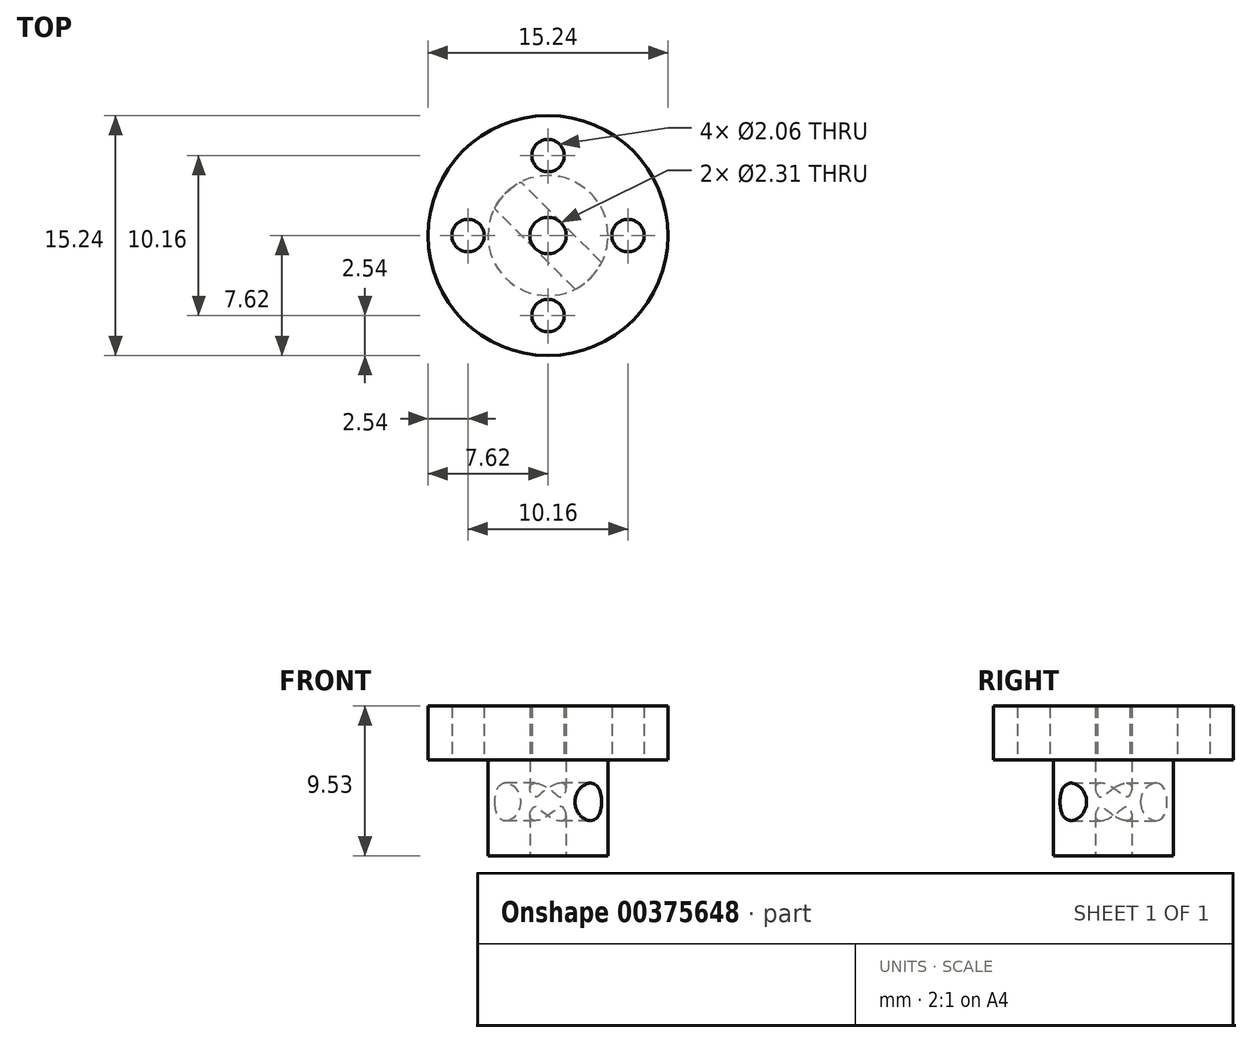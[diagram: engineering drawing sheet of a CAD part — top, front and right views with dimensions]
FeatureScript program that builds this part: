
annotation { "Feature Type Name" : "Feature", "Feature Type Description" : "" }
export const myFeature = defineFeature(function(context is Context, id is Id, definition is map)
    precondition{}
    {
        {
            var Q0;
            Q0=qCreatedBy(makeId("Front.planeOp"),FACE);
            var sketch = newSketch(context, id + "F0", { "sketchPlane" : qUnion([Q0])});
            skLineSegment(sketch, "E0", {"start": v(0, 9.3) * mm, "end": v(0, -5.66) * mm, "construction": true});
            skLineSegment(sketch, "E1", {"start": v(0, -3.43) * mm, "end": v(3.81, -3.43) * mm});
            skLineSegment(sketch, "E2", {"start": v(3.81, -3.43) * mm, "end": v(3.81, 2.67) * mm});
            skLineSegment(sketch, "E3", {"start": v(3.81, 2.67) * mm, "end": v(7.62, 2.67) * mm});
            skLineSegment(sketch, "E4", {"start": v(7.62, 2.67) * mm, "end": v(7.62, 6.1) * mm});
            skLineSegment(sketch, "E5", {"start": v(7.62, 6.1) * mm, "end": v(0, 6.1) * mm});
            skLineSegment(sketch, "E6", {"start": v(0, 6.1) * mm, "end": v(0, -3.43) * mm});
            skSolve(sketch);
        }
        {
            var Q0;
            Q0=makeQuery(id+"F0.imprint","IMPRINT",FACE,{"disambiguationData":[TD([[makeQuery(id+"F0.imprint","IMPRINT",EDGE,{"derivedFrom":sQuery(id+"F0.wireOp",EDGE,"E1")}),1.0]])]});
            var Q1;
            Q1=sQuery(id+"F0.wireOp",EDGE,"E0");
            revolve(context, id + "F1", {"entities" : qUnion([Q0]), "axis" : qUnion([Q1]), "revolveType" : RevolveType.FULL});
        }
        {
            var Q0;
            Q0=makeQuery(id+"F1.opRevolve","SWEPT_FACE",FACE,{"disambiguationData":[OSD([sQuery(id+"F0.wireOp",EDGE,"E1")])]});
            var sketch = newSketch(context, id + "F2", { "sketchPlane" : qUnion([Q0])});
            skCircle(sketch, "E7", {"center": v(0, 0) * mm, "radius": 1.16 * mm});
            skSolve(sketch);
        }
        {
            var Q0;
            Q0=makeQuery(id+"F2.imprint","IMPRINT",FACE,{"disambiguationData":[TD([[makeQuery(id+"F2.imprint","IMPRINT",EDGE,{"derivedFrom":sQuery(id+"F2.wireOp",EDGE,"E7")}),1.0]])]});
            extrude(context, id + "F3", {"entities" : qUnion([Q0]), "operationType" : NewBodyOperationType.REMOVE, "endBound" : BoundingType.UP_TO_NEXT, "oppositeDirection" : true, "depth" : 25.4 * mm});
        }
        {
            var Q0;
            Q0=qCreatedBy(makeId("Top.planeOp"),FACE);
            var sketch = newSketch(context, id + "F4", { "sketchPlane" : qUnion([Q0])});
            skCircle(sketch, "E8", {"center": v(0, 5.08) * mm, "radius": 1.03 * mm});
            skCircle(sketch, "E9", {"center": v(5.08, 0) * mm, "radius": 1.03 * mm});
            skCircle(sketch, "E10", {"center": v(-5.08, 0) * mm, "radius": 1.03 * mm});
            skCircle(sketch, "E11", {"center": v(0, -5.08) * mm, "radius": 1.03 * mm});
            skCircle(sketch, "E12", {"center": v(0, 0) * mm, "radius": 5.08 * mm, "construction": true});
            skSolve(sketch);
        }
        {
            var Q0;
            Q0 = qSketchRegion(id + "F4", true);
            extrude(context, id + "F5", {"entities" : qUnion([Q0]), "operationType" : NewBodyOperationType.REMOVE, "depth" : 25.4 * mm});
        }
        {
            var Q0;
            Q0=sQuery(id+"F0.wireOp",EDGE,"E6");
            cPlane(context, id + "F6", {"entities" : qUnion([Q0]), "cplaneType" : CPlaneType.LINE_ANGLE, "offset" : 25.4 * mm, "angle" : 45 * degree, "width" : 152.4 * mm, "height" : 152.4 * mm});
        }
        {
            var Q0;
            Q0=qCreatedBy(id+"F6.planeOp",FACE);
            var sketch = newSketch(context, id + "F7", { "sketchPlane" : qUnion([Q0])});
            skCircle(sketch, "E13", {"center": v(0, 0) * mm, "radius": 1.2 * mm});
            skSolve(sketch);
        }
        {
            var Q0;
            Q0 = qSketchRegion(id + "F7", true);
            extrude(context, id + "F8", {"entities" : qUnion([Q0]), "operationType" : NewBodyOperationType.REMOVE, "endBound" : BoundingType.SYMMETRIC, "oppositeDirection" : true, "depth" : 10.16 * mm});
        }
    });
